# Revit family: KRS_вытяжка
name_source: partatom
category: Воздухораспределители
revit_build: Autodesk Revit 2014 (Build: 20130308_1515(x64)
units: mm (PartAtom-declared; Revit-internal decimal feet)

## types (459) — shared parameters
A = 23 мм
URL = inplast.ru
margins = 13 мм
Изготовитель = ИНПЛАСТ
Материал = Алюминий_RAL9016 (INPLAST)
Описание = Потолочная растровая решетка
Тип крепежа = саморезы
zero-valued in all types: Вес, кг

## per-type parameters (varying)
| type | Aef | C | C' | D | D' | n1 | n2 |
| KRS 100х100-АL-RAL9016 | 0.006 м² | 100 мм | 96 мм | 100 мм | 96 мм | 7 | 7 |
| KRS 125х100-АL-RAL9016 | 0.008 м² | 125 мм | 121 мм | 100 мм | 96 мм | 9 | 7 |
| KRS 125х125-АL-RAL9016 | 0.009 м² | 125 мм | 121 мм | 125 мм | 121 мм | 9 | 9 |
| KRS 150х100-АL-RAL9016 | 0.009 м² | 150 мм | 146 мм | 100 мм | 96 мм | 11 | 7 |
| KRS 150х125-АL-RAL9016 | 0.011 м² | 150 мм | 146 мм | 125 мм | 121 мм | 11 | 9 |
| KRS 150х150-АL-RAL9016 | 0.014 м² | 150 мм | 146 мм | 150 мм | 146 мм | 11 | 11 |
| KRS 200х100-АL-RAL9016 | 0.012 м² | 200 мм | 196 мм | 100 мм | 96 мм | 14 | 7 |
| KRS 200х125-АL-RAL9016 | 0.015 м² | 200 мм | 196 мм | 125 мм | 121 мм | 14 | 9 |
| KRS 200х150-АL-RAL9016 | 0.018 м² | 200 мм | 196 мм | 150 мм | 146 мм | 14 | 11 |
| KRS 200х200-АL-RAL9016 | 0.024 м² | 200 мм | 196 мм | 200 мм | 196 мм | 14 | 14 |
| KRS 225х100-АL-RAL9016 | 0.014 м² | 225 мм | 221 мм | 100 мм | 96 мм | 16 | 7 |
| KRS 225х125-АL-RAL9016 | 0.017 м² | 225 мм | 221 мм | 125 мм | 121 мм | 16 | 9 |
| KRS 225х150-АL-RAL9016 | 0.020 м² | 225 мм | 221 мм | 150 мм | 146 мм | 16 | 11 |
| KRS 225х200-АL-RAL9016 | 0.027 м² | 225 мм | 221 мм | 200 мм | 196 мм | 16 | 14 |
| KRS 225х225-АL-RAL9016 | 0.030 м² | 225 мм | 221 мм | 225 мм | 221 мм | 16 | 16 |
| KRS 250х100-АL-RAL9016 | 0.015 м² | 250 мм | 246 мм | 100 мм | 96 мм | 18 | 7 |
| KRS 250х125-АL-RAL9016 | 0.019 м² | 250 мм | 246 мм | 125 мм | 121 мм | 18 | 9 |
| KRS 250х150-АL-RAL9016 | 0.023 м² | 250 мм | 246 мм | 150 мм | 146 мм | 18 | 11 |
| KRS 250х200-АL-RAL9016 | 0.030 м² | 250 мм | 246 мм | 200 мм | 196 мм | 18 | 14 |
| KRS 250х225-АL-RAL9016 | 0.034 м² | 250 мм | 246 мм | 225 мм | 221 мм | 18 | 16 |
| KRS 250х250-АL-RAL9016 | 0.038 м² | 250 мм | 246 мм | 250 мм | 246 мм | 18 | 18 |
| KRS 300х100-АL-RAL9016 | 0.018 м² | 300 мм | 296 мм | 100 мм | 96 мм | 21 | 7 |
| KRS 300х125-АL-RAL9016 | 0.023 м² | 300 мм | 296 мм | 125 мм | 121 мм | 21 | 9 |
| KRS 300х150-АL-RAL9016 | 0.027 м² | 300 мм | 296 мм | 150 мм | 146 мм | 21 | 11 |
| KRS 300х200-АL-RAL9016 | 0.036 м² | 300 мм | 296 мм | 200 мм | 196 мм | 21 | 14 |
| KRS 300х225-АL-RAL9016 | 0.041 м² | 300 мм | 296 мм | 225 мм | 221 мм | 21 | 16 |
| KRS 300х250-АL-RAL9016 | 0.045 м² | 300 мм | 296 мм | 250 мм | 246 мм | 21 | 18 |
| KRS 300х300-АL-RAL9016 | 0.054 м² | 300 мм | 296 мм | 300 мм | 296 мм | 21 | 21 |
| KRS 325х100-АL-RAL9016 | 0.020 м² | 325 мм | 321 мм | 100 мм | 96 мм | 23 | 7 |
| KRS 325х125-АL-RAL9016 | 0.024 м² | 325 мм | 321 мм | 125 мм | 121 мм | 23 | 9 |
| KRS 325х150-АL-RAL9016 | 0.029 м² | 325 мм | 321 мм | 150 мм | 146 мм | 23 | 11 |
| KRS 325х200-АL-RAL9016 | 0.039 м² | 325 мм | 321 мм | 200 мм | 196 мм | 23 | 14 |
| KRS 325х225-АL-RAL9016 | 0.044 м² | 325 мм | 321 мм | 225 мм | 221 мм | 23 | 16 |
| KRS 325х250-АL-RAL9016 | 0.049 м² | 325 мм | 321 мм | 250 мм | 246 мм | 23 | 18 |
| KRS 325х300-АL-RAL9016 | 0.059 м² | 325 мм | 321 мм | 300 мм | 296 мм | 23 | 21 |
| KRS 325х325-АL-RAL9016 | 0.064 м² | 325 мм | 321 мм | 325 мм | 321 мм | 23 | 23 |
| KRS 350х100-АL-RAL9016 | 0.021 м² | 350 мм | 346 мм | 100 мм | 96 мм | 25 | 7 |
| KRS 350х125-АL-RAL9016 | 0.026 м² | 350 мм | 346 мм | 125 мм | 121 мм | 25 | 9 |
| KRS 350х150-АL-RAL9016 | 0.032 м² | 350 мм | 346 мм | 150 мм | 146 мм | 25 | 11 |
| KRS 350х200-АL-RAL9016 | 0.042 м² | 350 мм | 346 мм | 200 мм | 196 мм | 25 | 14 |
| KRS 350х225-АL-RAL9016 | 0.047 м² | 350 мм | 346 мм | 225 мм | 221 мм | 25 | 16 |
| KRS 350х250-АL-RAL9016 | 0.053 м² | 350 мм | 346 мм | 250 мм | 246 мм | 25 | 18 |
| KRS 350х300-АL-RAL9016 | 0.063 м² | 350 мм | 346 мм | 300 мм | 296 мм | 25 | 21 |
| KRS 350х325-АL-RAL9016 | 0.068 м² | 350 мм | 346 мм | 325 мм | 321 мм | 25 | 23 |
| KRS 350х350-АL-RAL9016 | 0.074 м² | 350 мм | 346 мм | 350 мм | 346 мм | 25 | 25 |
| KRS 400х100-АL-RAL9016 | 0.024 м² | 400 мм | 396 мм | 100 мм | 96 мм | 29 | 7 |
| KRS 400х125-АL-RAL9016 | 0.030 м² | 400 мм | 396 мм | 125 мм | 121 мм | 29 | 9 |
| KRS 400х150-АL-RAL9016 | 0.036 м² | 400 мм | 396 мм | 150 мм | 146 мм | 29 | 11 |
| KRS 400х200-АL-RAL9016 | 0.048 м² | 400 мм | 396 мм | 200 мм | 196 мм | 29 | 14 |
| KRS 400х225-АL-RAL9016 | 0.054 м² | 400 мм | 396 мм | 225 мм | 221 мм | 29 | 16 |
| KRS 400х250-АL-RAL9016 | 0.060 м² | 400 мм | 396 мм | 250 мм | 246 мм | 29 | 18 |
| KRS 400х300-АL-RAL9016 | 0.072 м² | 400 мм | 396 мм | 300 мм | 296 мм | 29 | 21 |
| KRS 400х325-АL-RAL9016 | 0.078 м² | 400 мм | 396 мм | 325 мм | 321 мм | 29 | 23 |
| KRS 400х350-АL-RAL9016 | 0.084 м² | 400 мм | 396 мм | 350 мм | 346 мм | 29 | 25 |
| KRS 400х400-АL-RAL9016 | 0.096 м² | 400 мм | 396 мм | 400 мм | 396 мм | 29 | 29 |
| KRS 425х100-АL-RAL9016 | 0.026 м² | 425 мм | 421 мм | 100 мм | 96 мм | 30 | 7 |
| KRS 425х125-АL-RAL9016 | 0.032 м² | 425 мм | 421 мм | 125 мм | 121 мм | 30 | 9 |
| KRS 425х150-АL-RAL9016 | 0.038 м² | 425 мм | 421 мм | 150 мм | 146 мм | 30 | 11 |
| KRS 425х200-АL-RAL9016 | 0.051 м² | 425 мм | 421 мм | 200 мм | 196 мм | 30 | 14 |
| KRS 425х225-АL-RAL9016 | 0.058 м² | 425 мм | 421 мм | 225 мм | 221 мм | 30 | 16 |
| KRS 425х250-АL-RAL9016 | 0.064 м² | 425 мм | 421 мм | 250 мм | 246 мм | 30 | 18 |
| KRS 425х300-АL-RAL9016 | 0.077 м² | 425 мм | 421 мм | 300 мм | 296 мм | 30 | 21 |
| KRS 425х325-АL-RAL9016 | 0.083 м² | 425 мм | 421 мм | 325 мм | 321 мм | 30 | 23 |
| KRS 425х350-АL-RAL9016 | 0.089 м² | 425 мм | 421 мм | 350 мм | 346 мм | 30 | 25 |
| KRS 425х400-АL-RAL9016 | 0.102 м² | 425 мм | 421 мм | 400 мм | 396 мм | 30 | 29 |
| KRS 425х425-АL-RAL9016 | 0.109 м² | 425 мм | 421 мм | 425 мм | 421 мм | 30 | 30 |
| KRS 450х100-АL-RAL9016 | 0.027 м² | 450 мм | 446 мм | 100 мм | 96 мм | 32 | 7 |
| KRS 450х125-АL-RAL9016 | 0.034 м² | 450 мм | 446 мм | 125 мм | 121 мм | 32 | 9 |
| KRS 450х150-АL-RAL9016 | 0.041 м² | 450 мм | 446 мм | 150 мм | 146 мм | 32 | 11 |
| KRS 450х200-АL-RAL9016 | 0.054 м² | 450 мм | 446 мм | 200 мм | 196 мм | 32 | 14 |
| KRS 450х225-АL-RAL9016 | 0.061 м² | 450 мм | 446 мм | 225 мм | 221 мм | 32 | 16 |
| KRS 450х250-АL-RAL9016 | 0.068 м² | 450 мм | 446 мм | 250 мм | 246 мм | 32 | 18 |
| KRS 450х300-АL-RAL9016 | 0.081 м² | 450 мм | 446 мм | 300 мм | 296 мм | 32 | 21 |
| KRS 450х325-АL-RAL9016 | 0.088 м² | 450 мм | 446 мм | 325 мм | 321 мм | 32 | 23 |
| KRS 450х350-АL-RAL9016 | 0.095 м² | 450 мм | 446 мм | 350 мм | 346 мм | 32 | 25 |
| KRS 450х400-АL-RAL9016 | 0.108 м² | 450 мм | 446 мм | 400 мм | 396 мм | 32 | 29 |
| KRS 450х425-АL-RAL9016 | 0.115 м² | 450 мм | 446 мм | 425 мм | 421 мм | 32 | 30 |
| KRS 450х450-АL-RAL9016 | 0.122 м² | 450 мм | 446 мм | 450 мм | 446 мм | 32 | 32 |
| KRS 500х100-АL-RAL9016 | 0.030 м² | 500 мм | 496 мм | 100 мм | 96 мм | 36 | 7 |
| KRS 500х125-АL-RAL9016 | 0.038 м² | 500 мм | 496 мм | 125 мм | 121 мм | 36 | 9 |
| KRS 500х150-АL-RAL9016 | 0.045 м² | 500 мм | 496 мм | 150 мм | 146 мм | 36 | 11 |
| KRS 500х200-АL-RAL9016 | 0.060 м² | 500 мм | 496 мм | 200 мм | 196 мм | 36 | 14 |
| KRS 500х225-АL-RAL9016 | 0.068 м² | 500 мм | 496 мм | 225 мм | 221 мм | 36 | 16 |
| KRS 500х250-АL-RAL9016 | 0.075 м² | 500 мм | 496 мм | 250 мм | 246 мм | 36 | 18 |
| KRS 500х300-АL-RAL9016 | 0.090 м² | 500 мм | 496 мм | 300 мм | 296 мм | 36 | 21 |
| KRS 500х325-АL-RAL9016 | 0.098 м² | 500 мм | 496 мм | 325 мм | 321 мм | 36 | 23 |
| KRS 500х350-АL-RAL9016 | 0.105 м² | 500 мм | 496 мм | 350 мм | 346 мм | 36 | 25 |
| KRS 500х400-АL-RAL9016 | 0.120 м² | 500 мм | 496 мм | 400 мм | 396 мм | 36 | 29 |
| KRS 500х425-АL-RAL9016 | 0.128 м² | 500 мм | 496 мм | 425 мм | 421 мм | 36 | 30 |
| KRS 500х450-АL-RAL9016 | 0.135 м² | 500 мм | 496 мм | 450 мм | 446 мм | 36 | 32 |
| KRS 500х500-АL-RAL9016 | 0.150 м² | 500 мм | 496 мм | 500 мм | 496 мм | 36 | 36 |
| KRS 525х100-АL-RAL9016 | 0.032 м² | 525 мм | 521 мм | 100 мм | 96 мм | 38 | 7 |
| KRS 525х125-АL-RAL9016 | 0.039 м² | 525 мм | 521 мм | 125 мм | 121 мм | 38 | 9 |
| KRS 525х150-АL-RAL9016 | 0.047 м² | 525 мм | 521 мм | 150 мм | 146 мм | 38 | 11 |
| KRS 525х200-АL-RAL9016 | 0.063 м² | 525 мм | 521 мм | 200 мм | 196 мм | 38 | 14 |
| KRS 525х225-АL-RAL9016 | 0.071 м² | 525 мм | 521 мм | 225 мм | 221 мм | 38 | 16 |
| KRS 525х250-АL-RAL9016 | 0.079 м² | 525 мм | 521 мм | 250 мм | 246 мм | 38 | 18 |
| KRS 525х300-АL-RAL9016 | 0.095 м² | 525 мм | 521 мм | 300 мм | 296 мм | 38 | 21 |
| KRS 525х325-АL-RAL9016 | 0.103 м² | 525 мм | 521 мм | 325 мм | 321 мм | 38 | 23 |
| KRS 525х350-АL-RAL9016 | 0.111 м² | 525 мм | 521 мм | 350 мм | 346 мм | 38 | 25 |
| KRS 525х400-АL-RAL9016 | 0.126 м² | 525 мм | 521 мм | 400 мм | 396 мм | 38 | 29 |
| KRS 525х425-АL-RAL9016 | 0.134 м² | 525 мм | 521 мм | 425 мм | 421 мм | 38 | 30 |
| KRS 525х450-АL-RAL9016 | 0.142 м² | 525 мм | 521 мм | 450 мм | 446 мм | 38 | 32 |
| KRS 525х500-АL-RAL9016 | 0.158 м² | 525 мм | 521 мм | 500 мм | 496 мм | 38 | 36 |
| KRS 525х525-АL-RAL9016 | 0.166 м² | 525 мм | 521 мм | 525 мм | 521 мм | 38 | 38 |
| KRS 550х100-АL-RAL9016 | 0.033 м² | 550 мм | 546 мм | 100 мм | 96 мм | 39 | 7 |
| KRS 550х125-АL-RAL9016 | 0.041 м² | 550 мм | 546 мм | 125 мм | 121 мм | 39 | 9 |
| KRS 550х150-АL-RAL9016 | 0.050 м² | 550 мм | 546 мм | 150 мм | 146 мм | 39 | 11 |
| KRS 550х200-АL-RAL9016 | 0.066 м² | 550 мм | 546 мм | 200 мм | 196 мм | 39 | 14 |
| KRS 550х225-АL-RAL9016 | 0.074 м² | 550 мм | 546 мм | 225 мм | 221 мм | 39 | 16 |
| KRS 550х250-АL-RAL9016 | 0.083 м² | 550 мм | 546 мм | 250 мм | 246 мм | 39 | 18 |
| KRS 550х300-АL-RAL9016 | 0.099 м² | 550 мм | 546 мм | 300 мм | 296 мм | 39 | 21 |
| KRS 550х325-АL-RAL9016 | 0.108 м² | 550 мм | 546 мм | 325 мм | 321 мм | 39 | 23 |
| KRS 550х350-АL-RAL9016 | 0.116 м² | 550 мм | 546 мм | 350 мм | 346 мм | 39 | 25 |
| KRS 550х400-АL-RAL9016 | 0.132 м² | 550 мм | 546 мм | 400 мм | 396 мм | 39 | 29 |
| KRS 550х425-АL-RAL9016 | 0.141 м² | 550 мм | 546 мм | 425 мм | 421 мм | 39 | 30 |
| KRS 550х450-АL-RAL9016 | 0.149 м² | 550 мм | 546 мм | 450 мм | 446 мм | 39 | 32 |
| KRS 550х500-АL-RAL9016 | 0.165 м² | 550 мм | 546 мм | 500 мм | 496 мм | 39 | 36 |
| KRS 550х525-АL-RAL9016 | 0.174 м² | 550 мм | 546 мм | 525 мм | 521 мм | 39 | 38 |
| KRS 550х550-АL-RAL9016 | 0.182 м² | 550 мм | 546 мм | 550 мм | 546 мм | 39 | 39 |
| KRS 600х100-АL-RAL9016 | 0.036 м² | 600 мм | 596 мм | 100 мм | 96 мм | 43 | 7 |
| KRS 600х125-АL-RAL9016 | 0.045 м² | 600 мм | 596 мм | 125 мм | 121 мм | 43 | 9 |
| KRS 600х150-АL-RAL9016 | 0.054 м² | 600 мм | 596 мм | 150 мм | 146 мм | 43 | 11 |
| KRS 600х200-АL-RAL9016 | 0.072 м² | 600 мм | 596 мм | 200 мм | 196 мм | 43 | 14 |
| KRS 600х225-АL-RAL9016 | 0.081 м² | 600 мм | 596 мм | 225 мм | 221 мм | 43 | 16 |
| KRS 600х250-АL-RAL9016 | 0.090 м² | 600 мм | 596 мм | 250 мм | 246 мм | 43 | 18 |
| KRS 600х300-АL-RAL9016 | 0.108 м² | 600 мм | 596 мм | 300 мм | 296 мм | 43 | 21 |
| KRS 600х325-АL-RAL9016 | 0.117 м² | 600 мм | 596 мм | 325 мм | 321 мм | 43 | 23 |
| KRS 600х350-АL-RAL9016 | 0.126 м² | 600 мм | 596 мм | 350 мм | 346 мм | 43 | 25 |
| KRS 600х400-АL-RAL9016 | 0.144 м² | 600 мм | 596 мм | 400 мм | 396 мм | 43 | 29 |
| KRS 600х425-АL-RAL9016 | 0.153 м² | 600 мм | 596 мм | 425 мм | 421 мм | 43 | 30 |
| KRS 600х450-АL-RAL9016 | 0.162 м² | 600 мм | 596 мм | 450 мм | 446 мм | 43 | 32 |
| KRS 600х500-АL-RAL9016 | 0.180 м² | 600 мм | 596 мм | 500 мм | 496 мм | 43 | 36 |
| KRS 600х525-АL-RAL9016 | 0.190 м² | 600 мм | 596 мм | 525 мм | 521 мм | 43 | 38 |
| KRS 600х550-АL-RAL9016 | 0.199 м² | 600 мм | 596 мм | 550 мм | 546 мм | 43 | 39 |
| KRS 600х600-АL-RAL9016 | 0.217 м² | 600 мм | 596 мм | 600 мм | 596 мм | 43 | 43 |
| KRS 625х100-АL-RAL9016 | 0.038 м² | 625 мм | 621 мм | 100 мм | 96 мм | 45 | 7 |
| KRS 625х125-АL-RAL9016 | 0.047 м² | 625 мм | 621 мм | 125 мм | 121 мм | 45 | 9 |
| KRS 625х150-АL-RAL9016 | 0.056 м² | 625 мм | 621 мм | 150 мм | 146 мм | 45 | 11 |
| KRS 625х200-АL-RAL9016 | 0.075 м² | 625 мм | 621 мм | 200 мм | 196 мм | 45 | 14 |
| KRS 625х225-АL-RAL9016 | 0.085 м² | 625 мм | 621 мм | 225 мм | 221 мм | 45 | 16 |
| KRS 625х250-АL-RAL9016 | 0.094 м² | 625 мм | 621 мм | 250 мм | 246 мм | 45 | 18 |
| KRS 625х300-АL-RAL9016 | 0.113 м² | 625 мм | 621 мм | 300 мм | 296 мм | 45 | 21 |
| KRS 625х325-АL-RAL9016 | 0.122 м² | 625 мм | 621 мм | 325 мм | 321 мм | 45 | 23 |
| KRS 625х350-АL-RAL9016 | 0.132 м² | 625 мм | 621 мм | 350 мм | 346 мм | 45 | 25 |
| KRS 625х400-АL-RAL9016 | 0.150 м² | 625 мм | 621 мм | 400 мм | 396 мм | 45 | 29 |
| KRS 625х425-АL-RAL9016 | 0.160 м² | 625 мм | 621 мм | 425 мм | 421 мм | 45 | 30 |
| KRS 625х450-АL-RAL9016 | 0.169 м² | 625 мм | 621 мм | 450 мм | 446 мм | 45 | 32 |
| KRS 625х500-АL-RAL9016 | 0.188 м² | 625 мм | 621 мм | 500 мм | 496 мм | 45 | 36 |
| KRS 625х525-АL-RAL9016 | 0.197 м² | 625 мм | 621 мм | 525 мм | 521 мм | 45 | 38 |
| KRS 625х550-АL-RAL9016 | 0.207 м² | 625 мм | 621 мм | 550 мм | 546 мм | 45 | 39 |
| KRS 625х600-АL-RAL9016 | 0.226 м² | 625 мм | 621 мм | 600 мм | 596 мм | 45 | 43 |
| KRS 625х625-АL-RAL9016 | 0.235 м² | 625 мм | 621 мм | 625 мм | 621 мм | 45 | 45 |
| KRS 650х100-АL-RAL9016 | 0.039 м² | 650 мм | 646 мм | 100 мм | 96 мм | 46 | 7 |
| KRS 650х125-АL-RAL9016 | 0.049 м² | 650 мм | 646 мм | 125 мм | 121 мм | 46 | 9 |
| KRS 650х150-АL-RAL9016 | 0.059 м² | 650 мм | 646 мм | 150 мм | 146 мм | 46 | 11 |
| KRS 650х200-АL-RAL9016 | 0.078 м² | 650 мм | 646 мм | 200 мм | 196 мм | 46 | 14 |
| KRS 650х225-АL-RAL9016 | 0.088 м² | 650 мм | 646 мм | 225 мм | 221 мм | 46 | 16 |
| KRS 650х250-АL-RAL9016 | 0.098 м² | 650 мм | 646 мм | 250 мм | 246 мм | 46 | 18 |
| KRS 650х300-АL-RAL9016 | 0.117 м² | 650 мм | 646 мм | 300 мм | 296 мм | 46 | 21 |
| KRS 650х325-АL-RAL9016 | 0.127 м² | 650 мм | 646 мм | 325 мм | 321 мм | 46 | 23 |
| KRS 650х350-АL-RAL9016 | 0.137 м² | 650 мм | 646 мм | 350 мм | 346 мм | 46 | 25 |
| KRS 650х400-АL-RAL9016 | 0.156 м² | 650 мм | 646 мм | 400 мм | 396 мм | 46 | 29 |
| KRS 650х425-АL-RAL9016 | 0.166 м² | 650 мм | 646 мм | 425 мм | 421 мм | 46 | 30 |
| KRS 650х450-АL-RAL9016 | 0.176 м² | 650 мм | 646 мм | 450 мм | 446 мм | 46 | 32 |
| KRS 650х500-АL-RAL9016 | 0.196 м² | 650 мм | 646 мм | 500 мм | 496 мм | 46 | 36 |
| KRS 650х525-АL-RAL9016 | 0.205 м² | 650 мм | 646 мм | 525 мм | 521 мм | 46 | 38 |
| KRS 650х550-АL-RAL9016 | 0.215 м² | 650 мм | 646 мм | 550 мм | 546 мм | 46 | 39 |
| KRS 650х600-АL-RAL9016 | 0.235 м² | 650 мм | 646 мм | 600 мм | 596 мм | 46 | 43 |
| KRS 650х625-АL-RAL9016 | 0.244 м² | 650 мм | 646 мм | 625 мм | 621 мм | 46 | 45 |
| KRS 700х100-АL-RAL9016 | 0.042 м² | 700 мм | 696 мм | 100 мм | 96 мм | 50 | 7 |
| KRS 700х125-АL-RAL9016 | 0.053 м² | 700 мм | 696 мм | 125 мм | 121 мм | 50 | 9 |
| KRS 700х150-АL-RAL9016 | 0.063 м² | 700 мм | 696 мм | 150 мм | 146 мм | 50 | 11 |
| KRS 700х200-АL-RAL9016 | 0.084 м² | 700 мм | 696 мм | 200 мм | 196 мм | 50 | 14 |
| KRS 700х225-АL-RAL9016 | 0.095 м² | 700 мм | 696 мм | 225 мм | 221 мм | 50 | 16 |
| KRS 700х250-АL-RAL9016 | 0.105 м² | 700 мм | 696 мм | 250 мм | 246 мм | 50 | 18 |
| KRS 700х300-АL-RAL9016 | 0.126 м² | 700 мм | 696 мм | 300 мм | 296 мм | 50 | 21 |
| KRS 700х325-АL-RAL9016 | 0.137 м² | 700 мм | 696 мм | 325 мм | 321 мм | 50 | 23 |
| KRS 700х350-АL-RAL9016 | 0.147 м² | 700 мм | 696 мм | 350 мм | 346 мм | 50 | 25 |
| KRS 700х400-АL-RAL9016 | 0.168 м² | 700 мм | 696 мм | 400 мм | 396 мм | 50 | 29 |
| KRS 700х425-АL-RAL9016 | 0.179 м² | 700 мм | 696 мм | 425 мм | 421 мм | 50 | 30 |
| KRS 700х450-АL-RAL9016 | 0.190 м² | 700 мм | 696 мм | 450 мм | 446 мм | 50 | 32 |
| KRS 700х500-АL-RAL9016 | 0.211 м² | 700 мм | 696 мм | 500 мм | 496 мм | 50 | 36 |
| KRS 700х525-АL-RAL9016 | 0.221 м² | 700 мм | 696 мм | 525 мм | 521 мм | 50 | 38 |
| KRS 700х550-АL-RAL9016 | 0.232 м² | 700 мм | 696 мм | 550 мм | 546 мм | 50 | 39 |
| KRS 700х600-АL-RAL9016 | 0.253 м² | 700 мм | 696 мм | 600 мм | 596 мм | 50 | 43 |
| KRS 700х625-АL-RAL9016 | 0.263 м² | 700 мм | 696 мм | 625 мм | 621 мм | 50 | 45 |
| KRS 725х100-АL-RAL9016 | 0.044 м² | 725 мм | 721 мм | 100 мм | 96 мм | 52 | 7 |
| KRS 725х125-АL-RAL9016 | 0.055 м² | 725 мм | 721 мм | 125 мм | 121 мм | 52 | 9 |
| KRS 725х150-АL-RAL9016 | 0.065 м² | 725 мм | 721 мм | 150 мм | 146 мм | 52 | 11 |
| KRS 725х200-АL-RAL9016 | 0.087 м² | 725 мм | 721 мм | 200 мм | 196 мм | 52 | 14 |
| KRS 725х225-АL-RAL9016 | 0.098 м² | 725 мм | 721 мм | 225 мм | 221 мм | 52 | 16 |
| KRS 725х250-АL-RAL9016 | 0.109 м² | 725 мм | 721 мм | 250 мм | 246 мм | 52 | 18 |
| KRS 725х300-АL-RAL9016 | 0.131 м² | 725 мм | 721 мм | 300 мм | 296 мм | 52 | 21 |
| KRS 725х325-АL-RAL9016 | 0.142 м² | 725 мм | 721 мм | 325 мм | 321 мм | 52 | 23 |
| KRS 725х350-АL-RAL9016 | 0.153 м² | 725 мм | 721 мм | 350 мм | 346 мм | 52 | 25 |
| KRS 725х400-АL-RAL9016 | 0.174 м² | 725 мм | 721 мм | 400 мм | 396 мм | 52 | 29 |
| KRS 725х425-АL-RAL9016 | 0.185 м² | 725 мм | 721 мм | 425 мм | 421 мм | 52 | 30 |
| KRS 725х450-АL-RAL9016 | 0.196 м² | 725 мм | 721 мм | 450 мм | 446 мм | 52 | 32 |
| KRS 725х500-АL-RAL9016 | 0.218 м² | 725 мм | 721 мм | 500 мм | 496 мм | 52 | 36 |
| KRS 725х525-АL-RAL9016 | 0.229 м² | 725 мм | 721 мм | 525 мм | 521 мм | 52 | 38 |
| KRS 725х550-АL-RAL9016 | 0.240 м² | 725 мм | 721 мм | 550 мм | 546 мм | 52 | 39 |
| KRS 725х600-АL-RAL9016 | 0.262 м² | 725 мм | 721 мм | 600 мм | 596 мм | 52 | 43 |
| KRS 725х625-АL-RAL9016 | 0.273 м² | 725 мм | 721 мм | 625 мм | 621 мм | 52 | 45 |
| KRS 750х100-АL-RAL9016 | 0.045 м² | 750 мм | 746 мм | 100 мм | 96 мм | 54 | 7 |
| KRS 750х125-АL-RAL9016 | 0.056 м² | 750 мм | 746 мм | 125 мм | 121 мм | 54 | 9 |
| KRS 750х150-АL-RAL9016 | 0.068 м² | 750 мм | 746 мм | 150 мм | 146 мм | 54 | 11 |
| KRS 750х200-АL-RAL9016 | 0.090 м² | 750 мм | 746 мм | 200 мм | 196 мм | 54 | 14 |
| KRS 750х225-АL-RAL9016 | 0.102 м² | 750 мм | 746 мм | 225 мм | 221 мм | 54 | 16 |
| KRS 750х250-АL-RAL9016 | 0.113 м² | 750 мм | 746 мм | 250 мм | 246 мм | 54 | 18 |
| KRS 750х300-АL-RAL9016 | 0.135 м² | 750 мм | 746 мм | 300 мм | 296 мм | 54 | 21 |
| KRS 750х325-АL-RAL9016 | 0.147 м² | 750 мм | 746 мм | 325 мм | 321 мм | 54 | 23 |
| KRS 750х350-АL-RAL9016 | 0.158 м² | 750 мм | 746 мм | 350 мм | 346 мм | 54 | 25 |
| KRS 750х400-АL-RAL9016 | 0.180 м² | 750 мм | 746 мм | 400 мм | 396 мм | 54 | 29 |
| KRS 750х425-АL-RAL9016 | 0.192 м² | 750 мм | 746 мм | 425 мм | 421 мм | 54 | 30 |
| KRS 750х450-АL-RAL9016 | 0.203 м² | 750 мм | 746 мм | 450 мм | 446 мм | 54 | 32 |
| KRS 750х500-АL-RAL9016 | 0.226 м² | 750 мм | 746 мм | 500 мм | 496 мм | 54 | 36 |
| KRS 750х525-АL-RAL9016 | 0.237 м² | 750 мм | 746 мм | 525 мм | 521 мм | 54 | 38 |
| KRS 750х550-АL-RAL9016 | 0.248 м² | 750 мм | 746 мм | 550 мм | 546 мм | 54 | 39 |
| KRS 750х600-АL-RAL9016 | 0.271 м² | 750 мм | 746 мм | 600 мм | 596 мм | 54 | 43 |
| KRS 750х625-АL-RAL9016 | 0.282 м² | 750 мм | 746 мм | 625 мм | 621 мм | 54 | 45 |
| KRS 800х100-АL-RAL9016 | 0.048 м² | 800 мм | 796 мм | 100 мм | 96 мм | 57 | 7 |
| KRS 800х125-АL-RAL9016 | 0.060 м² | 800 мм | 796 мм | 125 мм | 121 мм | 57 | 9 |
| KRS 800х150-АL-RAL9016 | 0.072 м² | 800 мм | 796 мм | 150 мм | 146 мм | 57 | 11 |
| KRS 800х200-АL-RAL9016 | 0.096 м² | 800 мм | 796 мм | 200 мм | 196 мм | 57 | 14 |
| KRS 800х225-АL-RAL9016 | 0.108 м² | 800 мм | 796 мм | 225 мм | 221 мм | 57 | 16 |
| KRS 800х250-АL-RAL9016 | 0.120 м² | 800 мм | 796 мм | 250 мм | 246 мм | 57 | 18 |
| KRS 800х300-АL-RAL9016 | 0.144 м² | 800 мм | 796 мм | 300 мм | 296 мм | 57 | 21 |
| KRS 800х325-АL-RAL9016 | 0.156 м² | 800 мм | 796 мм | 325 мм | 321 мм | 57 | 23 |
| KRS 800х350-АL-RAL9016 | 0.168 м² | 800 мм | 796 мм | 350 мм | 346 мм | 57 | 25 |
| KRS 800х400-АL-RAL9016 | 0.193 м² | 800 мм | 796 мм | 400 мм | 396 мм | 57 | 29 |
| KRS 800х425-АL-RAL9016 | 0.205 м² | 800 мм | 796 мм | 425 мм | 421 мм | 57 | 30 |
| KRS 800х450-АL-RAL9016 | 0.217 м² | 800 мм | 796 мм | 450 мм | 446 мм | 57 | 32 |
| KRS 800х500-АL-RAL9016 | 0.241 м² | 800 мм | 796 мм | 500 мм | 496 мм | 57 | 36 |
| KRS 800х525-АL-RAL9016 | 0.253 м² | 800 мм | 796 мм | 525 мм | 521 мм | 57 | 38 |
| KRS 800х550-АL-RAL9016 | 0.265 м² | 800 мм | 796 мм | 550 мм | 546 мм | 57 | 39 |
| KRS 800х600-АL-RAL9016 | 0.289 м² | 800 мм | 796 мм | 600 мм | 596 мм | 57 | 43 |
| KRS 800х625-АL-RAL9016 | 0.301 м² | 800 мм | 796 мм | 625 мм | 621 мм | 57 | 45 |
| KRS 825х100-АL-RAL9016 | 0.050 м² | 825 мм | 821 мм | 100 мм | 96 мм | 59 | 7 |
| KRS 825х125-АL-RAL9016 | 0.062 м² | 825 мм | 821 мм | 125 мм | 121 мм | 59 | 9 |
| KRS 825х150-АL-RAL9016 | 0.074 м² | 825 мм | 821 мм | 150 мм | 146 мм | 59 | 11 |
| KRS 825х200-АL-RAL9016 | 0.099 м² | 825 мм | 821 мм | 200 мм | 196 мм | 59 | 14 |
| KRS 825х225-АL-RAL9016 | 0.112 м² | 825 мм | 821 мм | 225 мм | 221 мм | 59 | 16 |
| KRS 825х250-АL-RAL9016 | 0.124 м² | 825 мм | 821 мм | 250 мм | 246 мм | 59 | 18 |
| KRS 825х300-АL-RAL9016 | 0.149 м² | 825 мм | 821 мм | 300 мм | 296 мм | 59 | 21 |
| KRS 825х325-АL-RAL9016 | 0.161 м² | 825 мм | 821 мм | 325 мм | 321 мм | 59 | 23 |
| KRS 825х350-АL-RAL9016 | 0.174 м² | 825 мм | 821 мм | 350 мм | 346 мм | 59 | 25 |
| KRS 825х400-АL-RAL9016 | 0.199 м² | 825 мм | 821 мм | 400 мм | 396 мм | 59 | 29 |
| KRS 825х425-АL-RAL9016 | 0.211 м² | 825 мм | 821 мм | 425 мм | 421 мм | 59 | 30 |
| KRS 825х450-АL-RAL9016 | 0.223 м² | 825 мм | 821 мм | 450 мм | 446 мм | 59 | 32 |
| KRS 825х500-АL-RAL9016 | 0.248 м² | 825 мм | 821 мм | 500 мм | 496 мм | 59 | 36 |
| KRS 825х525-АL-RAL9016 | 0.261 м² | 825 мм | 821 мм | 525 мм | 521 мм | 59 | 38 |
| KRS 825х550-АL-RAL9016 | 0.273 м² | 825 мм | 821 мм | 550 мм | 546 мм | 59 | 39 |
| KRS 825х600-АL-RAL9016 | 0.298 м² | 825 мм | 821 мм | 600 мм | 596 мм | 59 | 43 |
| KRS 825х625-АL-RAL9016 | 0.310 м² | 825 мм | 821 мм | 625 мм | 621 мм | 59 | 45 |
| KRS 850х100-АL-RAL9016 | 0.051 м² | 850 мм | 846 мм | 100 мм | 96 мм | 61 | 7 |
| KRS 850х125-АL-RAL9016 | 0.064 м² | 850 мм | 846 мм | 125 мм | 121 мм | 61 | 9 |
| KRS 850х150-АL-RAL9016 | 0.077 м² | 850 мм | 846 мм | 150 мм | 146 мм | 61 | 11 |
| KRS 850х200-АL-RAL9016 | 0.102 м² | 850 мм | 846 мм | 200 мм | 196 мм | 61 | 14 |
| KRS 850х225-АL-RAL9016 | 0.115 м² | 850 мм | 846 мм | 225 мм | 221 мм | 61 | 16 |
| KRS 850х250-АL-RAL9016 | 0.128 м² | 850 мм | 846 мм | 250 мм | 246 мм | 61 | 18 |
| KRS 850х300-АL-RAL9016 | 0.153 м² | 850 мм | 846 мм | 300 мм | 296 мм | 61 | 21 |
| KRS 850х325-АL-RAL9016 | 0.166 м² | 850 мм | 846 мм | 325 мм | 321 мм | 61 | 23 |
| KRS 850х350-АL-RAL9016 | 0.179 м² | 850 мм | 846 мм | 350 мм | 346 мм | 61 | 25 |
| KRS 850х400-АL-RAL9016 | 0.205 м² | 850 мм | 846 мм | 400 мм | 396 мм | 61 | 29 |
| KRS 850х425-АL-RAL9016 | 0.217 м² | 850 мм | 846 мм | 425 мм | 421 мм | 61 | 30 |
| KRS 850х450-АL-RAL9016 | 0.230 м² | 850 мм | 846 мм | 450 мм | 446 мм | 61 | 32 |
| KRS 850х500-АL-RAL9016 | 0.256 м² | 850 мм | 846 мм | 500 мм | 496 мм | 61 | 36 |
| KRS 850х525-АL-RAL9016 | 0.268 м² | 850 мм | 846 мм | 525 мм | 521 мм | 61 | 38 |
| KRS 850х550-АL-RAL9016 | 0.281 м² | 850 мм | 846 мм | 550 мм | 546 мм | 61 | 39 |
| KRS 850х600-АL-RAL9016 | 0.307 м² | 850 мм | 846 мм | 600 мм | 596 мм | 61 | 43 |
| KRS 850х625-АL-RAL9016 | 0.320 м² | 850 мм | 846 мм | 625 мм | 621 мм | 61 | 45 |
| KRS 900х100-АL-RAL9016 | 0.054 м² | 900 мм | 896 мм | 100 мм | 96 мм | 64 | 7 |
| KRS 900х125-АL-RAL9016 | 0.068 м² | 900 мм | 896 мм | 125 мм | 121 мм | 64 | 9 |
| KRS 900х150-АL-RAL9016 | 0.081 м² | 900 мм | 896 мм | 150 мм | 146 мм | 64 | 11 |
| KRS 900х200-АL-RAL9016 | 0.108 м² | 900 мм | 896 мм | 200 мм | 196 мм | 64 | 14 |
| KRS 900х225-АL-RAL9016 | 0.122 м² | 900 мм | 896 мм | 225 мм | 221 мм | 64 | 16 |
| KRS 900х250-АL-RAL9016 | 0.135 м² | 900 мм | 896 мм | 250 мм | 246 мм | 64 | 18 |
| KRS 900х300-АL-RAL9016 | 0.162 м² | 900 мм | 896 мм | 300 мм | 296 мм | 64 | 21 |
| KRS 900х325-АL-RAL9016 | 0.176 м² | 900 мм | 896 мм | 325 мм | 321 мм | 64 | 23 |
| KRS 900х350-АL-RAL9016 | 0.190 м² | 900 мм | 896 мм | 350 мм | 346 мм | 64 | 25 |
| KRS 900х400-АL-RAL9016 | 0.217 м² | 900 мм | 896 мм | 400 мм | 396 мм | 64 | 29 |
| KRS 900х425-АL-RAL9016 | 0.230 м² | 900 мм | 896 мм | 425 мм | 421 мм | 64 | 30 |
| KRS 900х450-АL-RAL9016 | 0.244 м² | 900 мм | 896 мм | 450 мм | 446 мм | 64 | 32 |
| KRS 900х500-АL-RAL9016 | 0.271 м² | 900 мм | 896 мм | 500 мм | 496 мм | 64 | 36 |
| KRS 900х525-АL-RAL9016 | 0.284 м² | 900 мм | 896 мм | 525 мм | 521 мм | 64 | 38 |
| KRS 900х550-АL-RAL9016 | 0.298 м² | 900 мм | 896 мм | 550 мм | 546 мм | 64 | 39 |
| KRS 900х600-АL-RAL9016 | 0.325 м² | 900 мм | 896 мм | 600 мм | 596 мм | 64 | 43 |
| KRS 900х625-АL-RAL9016 | 0.338 м² | 900 мм | 896 мм | 625 мм | 621 мм | 64 | 45 |
| KRS 925х100-АL-RAL9016 | 0.056 м² | 925 мм | 921 мм | 100 мм | 96 мм | 66 | 7 |
| KRS 925х125-АL-RAL9016 | 0.070 м² | 925 мм | 921 мм | 125 мм | 121 мм | 66 | 9 |
| KRS 925х150-АL-RAL9016 | 0.083 м² | 925 мм | 921 мм | 150 мм | 146 мм | 66 | 11 |
| KRS 925х200-АL-RAL9016 | 0.111 м² | 925 мм | 921 мм | 200 мм | 196 мм | 66 | 14 |
| KRS 925х225-АL-RAL9016 | 0.125 м² | 925 мм | 921 мм | 225 мм | 221 мм | 66 | 16 |
| KRS 925х250-АL-RAL9016 | 0.139 м² | 925 мм | 921 мм | 250 мм | 246 мм | 66 | 18 |
| KRS 925х300-АL-RAL9016 | 0.167 м² | 925 мм | 921 мм | 300 мм | 296 мм | 66 | 21 |
| KRS 925х325-АL-RAL9016 | 0.181 м² | 925 мм | 921 мм | 325 мм | 321 мм | 66 | 23 |
| KRS 925х350-АL-RAL9016 | 0.195 м² | 925 мм | 921 мм | 350 мм | 346 мм | 66 | 25 |
| KRS 925х400-АL-RAL9016 | 0.223 м² | 925 мм | 921 мм | 400 мм | 396 мм | 66 | 29 |
| KRS 925х425-АL-RAL9016 | 0.237 м² | 925 мм | 921 мм | 425 мм | 421 мм | 66 | 30 |
| KRS 925х450-АL-RAL9016 | 0.250 м² | 925 мм | 921 мм | 450 мм | 446 мм | 66 | 32 |
| KRS 925х500-АL-RAL9016 | 0.278 м² | 925 мм | 921 мм | 500 мм | 496 мм | 66 | 36 |
| KRS 925х525-АL-RAL9016 | 0.292 м² | 925 мм | 921 мм | 525 мм | 521 мм | 66 | 38 |
| KRS 925х550-АL-RAL9016 | 0.306 м² | 925 мм | 921 мм | 550 мм | 546 мм | 66 | 39 |
| KRS 925х600-АL-RAL9016 | 0.334 м² | 925 мм | 921 мм | 600 мм | 596 мм | 66 | 43 |
| KRS 925х625-АL-RAL9016 | 0.348 м² | 925 мм | 921 мм | 625 мм | 621 мм | 66 | 45 |
| KRS 950х100-АL-RAL9016 | 0.057 м² | 950 мм | 946 мм | 100 мм | 96 мм | 68 | 7 |
| KRS 950х125-АL-RAL9016 | 0.071 м² | 950 мм | 946 мм | 125 мм | 121 мм | 68 | 9 |
| KRS 950х150-АL-RAL9016 | 0.086 м² | 950 мм | 946 мм | 150 мм | 146 мм | 68 | 11 |
| KRS 950х200-АL-RAL9016 | 0.114 м² | 950 мм | 946 мм | 200 мм | 196 мм | 68 | 14 |
| KRS 950х225-АL-RAL9016 | 0.129 м² | 950 мм | 946 мм | 225 мм | 221 мм | 68 | 16 |
| KRS 950х250-АL-RAL9016 | 0.143 м² | 950 мм | 946 мм | 250 мм | 246 мм | 68 | 18 |
| KRS 950х300-АL-RAL9016 | 0.171 м² | 950 мм | 946 мм | 300 мм | 296 мм | 68 | 21 |
| KRS 950х325-АL-RAL9016 | 0.186 м² | 950 мм | 946 мм | 325 мм | 321 мм | 68 | 23 |
| KRS 950х350-АL-RAL9016 | 0.200 м² | 950 мм | 946 мм | 350 мм | 346 мм | 68 | 25 |
| KRS 950х400-АL-RAL9016 | 0.229 м² | 950 мм | 946 мм | 400 мм | 396 мм | 68 | 29 |
| KRS 950х425-АL-RAL9016 | 0.243 м² | 950 мм | 946 мм | 425 мм | 421 мм | 68 | 30 |
| KRS 950х450-АL-RAL9016 | 0.257 м² | 950 мм | 946 мм | 450 мм | 446 мм | 68 | 32 |
| KRS 950х500-АL-RAL9016 | 0.286 м² | 950 мм | 946 мм | 500 мм | 496 мм | 68 | 36 |
| KRS 950х525-АL-RAL9016 | 0.300 м² | 950 мм | 946 мм | 525 мм | 521 мм | 68 | 38 |
| KRS 950х550-АL-RAL9016 | 0.314 м² | 950 мм | 946 мм | 550 мм | 546 мм | 68 | 39 |
| KRS 950х600-АL-RAL9016 | 0.343 м² | 950 мм | 946 мм | 600 мм | 596 мм | 68 | 43 |
| KRS 950х625-АL-RAL9016 | 0.357 м² | 950 мм | 946 мм | 625 мм | 621 мм | 68 | 45 |
| KRS 1000х100-АL-RAL9016 | 0.060 м² | 1000 мм | 996 мм | 100 мм | 96 мм | 71 | 7 |
| KRS 1000х125-АL-RAL9016 | 0.075 м² | 1000 мм | 996 мм | 125 мм | 121 мм | 71 | 9 |
| KRS 1000х150-АL-RAL9016 | 0.090 м² | 1000 мм | 996 мм | 150 мм | 146 мм | 71 | 11 |
| KRS 1000х200-АL-RAL9016 | 0.120 м² | 1000 мм | 996 мм | 200 мм | 196 мм | 71 | 14 |
| KRS 1000х225-АL-RAL9016 | 0.135 м² | 1000 мм | 996 мм | 225 мм | 221 мм | 71 | 16 |
| KRS 1000х250-АL-RAL9016 | 0.150 м² | 1000 мм | 996 мм | 250 мм | 246 мм | 71 | 18 |
| KRS 1000х300-АL-RAL9016 | 0.180 м² | 1000 мм | 996 мм | 300 мм | 296 мм | 71 | 21 |
| KRS 1000х325-АL-RAL9016 | 0.196 м² | 1000 мм | 996 мм | 325 мм | 321 мм | 71 | 23 |
| KRS 1000х350-АL-RAL9016 | 0.211 м² | 1000 мм | 996 мм | 350 мм | 346 мм | 71 | 25 |
| KRS 1000х400-АL-RAL9016 | 0.241 м² | 1000 мм | 996 мм | 400 мм | 396 мм | 71 | 29 |
| KRS 1000х425-АL-RAL9016 | 0.256 м² | 1000 мм | 996 мм | 425 мм | 421 мм | 71 | 30 |
| KRS 1000х450-АL-RAL9016 | 0.271 м² | 1000 мм | 996 мм | 450 мм | 446 мм | 71 | 32 |
| KRS 1000х500-АL-RAL9016 | 0.301 м² | 1000 мм | 996 мм | 500 мм | 496 мм | 71 | 36 |
| KRS 1000х525-АL-RAL9016 | 0.316 м² | 1000 мм | 996 мм | 525 мм | 521 мм | 71 | 38 |
| KRS 1000х550-АL-RAL9016 | 0.331 м² | 1000 мм | 996 мм | 550 мм | 546 мм | 71 | 39 |
| KRS 1000х600-АL-RAL9016 | 0.361 м² | 1000 мм | 996 мм | 600 мм | 596 мм | 71 | 43 |
| KRS 1000х625-АL-RAL9016 | 0.376 м² | 1000 мм | 996 мм | 625 мм | 621 мм | 71 | 45 |
| KRS 1025х100-АL-RAL9016 | 0.062 м² | 1025 мм | 1021 мм | 100 мм | 96 мм | 73 | 7 |
| KRS 1025х125-АL-RAL9016 | 0.077 м² | 1025 мм | 1021 мм | 125 мм | 121 мм | 73 | 9 |
| KRS 1025х150-АL-RAL9016 | 0.092 м² | 1025 мм | 1021 мм | 150 мм | 146 мм | 73 | 11 |
| KRS 1025х200-АL-RAL9016 | 0.123 м² | 1025 мм | 1021 мм | 200 мм | 196 мм | 73 | 14 |
| KRS 1025х225-АL-RAL9016 | 0.139 м² | 1025 мм | 1021 мм | 225 мм | 221 мм | 73 | 16 |
| KRS 1025х250-АL-RAL9016 | 0.154 м² | 1025 мм | 1021 мм | 250 мм | 246 мм | 73 | 18 |
| KRS 1025х300-АL-RAL9016 | 0.185 м² | 1025 мм | 1021 мм | 300 мм | 296 мм | 73 | 21 |
| KRS 1025х325-АL-RAL9016 | 0.200 м² | 1025 мм | 1021 мм | 325 мм | 321 мм | 73 | 23 |
| KRS 1025х350-АL-RAL9016 | 0.216 м² | 1025 мм | 1021 мм | 350 мм | 346 мм | 73 | 25 |
| KRS 1025х400-АL-RAL9016 | 0.247 м² | 1025 мм | 1021 мм | 400 мм | 396 мм | 73 | 29 |
| KRS 1025х425-АL-RAL9016 | 0.262 м² | 1025 мм | 1021 мм | 425 мм | 421 мм | 73 | 30 |
| KRS 1025х450-АL-RAL9016 | 0.277 м² | 1025 мм | 1021 мм | 450 мм | 446 мм | 73 | 32 |
| KRS 1025х500-АL-RAL9016 | 0.308 м² | 1025 мм | 1021 мм | 500 мм | 496 мм | 73 | 36 |
| KRS 1025х525-АL-RAL9016 | 0.324 м² | 1025 мм | 1021 мм | 525 мм | 521 мм | 73 | 38 |
| KRS 1025х550-АL-RAL9016 | 0.339 м² | 1025 мм | 1021 мм | 550 мм | 546 мм | 73 | 39 |
| KRS 1025х600-АL-RAL9016 | 0.370 м² | 1025 мм | 1021 мм | 600 мм | 596 мм | 73 | 43 |
| KRS 1025х625-АL-RAL9016 | 0.385 м² | 1025 мм | 1021 мм | 625 мм | 621 мм | 73 | 45 |
| KRS 1050х100-АL-RAL9016 | 0.063 м² | 1050 мм | 1046 мм | 100 мм | 96 мм | 75 | 7 |
| KRS 1050х125-АL-RAL9016 | 0.079 м² | 1050 мм | 1046 мм | 125 мм | 121 мм | 75 | 9 |
| KRS 1050х150-АL-RAL9016 | 0.095 м² | 1050 мм | 1046 мм | 150 мм | 146 мм | 75 | 11 |
| KRS 1050х200-АL-RAL9016 | 0.126 м² | 1050 мм | 1046 мм | 200 мм | 196 мм | 75 | 14 |
| KRS 1050х225-АL-RAL9016 | 0.142 м² | 1050 мм | 1046 мм | 225 мм | 221 мм | 75 | 16 |
| KRS 1050х250-АL-RAL9016 | 0.158 м² | 1050 мм | 1046 мм | 250 мм | 246 мм | 75 | 18 |
| KRS 1050х300-АL-RAL9016 | 0.190 м² | 1050 мм | 1046 мм | 300 мм | 296 мм | 75 | 21 |
| KRS 1050х325-АL-RAL9016 | 0.205 м² | 1050 мм | 1046 мм | 325 мм | 321 мм | 75 | 23 |
| KRS 1050х350-АL-RAL9016 | 0.221 м² | 1050 мм | 1046 мм | 350 мм | 346 мм | 75 | 25 |
| KRS 1050х400-АL-RAL9016 | 0.253 м² | 1050 мм | 1046 мм | 400 мм | 396 мм | 75 | 29 |
| KRS 1050х425-АL-RAL9016 | 0.268 м² | 1050 мм | 1046 мм | 425 мм | 421 мм | 75 | 30 |
| KRS 1050х450-АL-RAL9016 | 0.284 м² | 1050 мм | 1046 мм | 450 мм | 446 мм | 75 | 32 |
| KRS 1050х500-АL-RAL9016 | 0.316 м² | 1050 мм | 1046 мм | 500 мм | 496 мм | 75 | 36 |
| KRS 1050х525-АL-RAL9016 | 0.332 м² | 1050 мм | 1046 мм | 525 мм | 521 мм | 75 | 38 |
| KRS 1050х550-АL-RAL9016 | 0.347 м² | 1050 мм | 1046 мм | 550 мм | 546 мм | 75 | 39 |
| KRS 1050х600-АL-RAL9016 | 0.379 м² | 1050 мм | 1046 мм | 600 мм | 596 мм | 75 | 43 |
| KRS 1050х625-АL-RAL9016 | 0.395 м² | 1050 мм | 1046 мм | 625 мм | 621 мм | 75 | 45 |
| KRS 1100х100-АL-RAL9016 | 0.066 м² | 1100 мм | 1096 мм | 100 мм | 96 мм | 79 | 7 |
| KRS 1100х125-АL-RAL9016 | 0.083 м² | 1100 мм | 1096 мм | 125 мм | 121 мм | 79 | 9 |
| KRS 1100х150-АL-RAL9016 | 0.099 м² | 1100 мм | 1096 мм | 150 мм | 146 мм | 79 | 11 |
| KRS 1100х200-АL-RAL9016 | 0.132 м² | 1100 мм | 1096 мм | 200 мм | 196 мм | 79 | 14 |
| KRS 1100х225-АL-RAL9016 | 0.149 м² | 1100 мм | 1096 мм | 225 мм | 221 мм | 79 | 16 |
| KRS 1100х250-АL-RAL9016 | 0.165 м² | 1100 мм | 1096 мм | 250 мм | 246 мм | 79 | 18 |
| KRS 1100х300-АL-RAL9016 | 0.199 м² | 1100 мм | 1096 мм | 300 мм | 296 мм | 79 | 21 |
| KRS 1100х325-АL-RAL9016 | 0.215 м² | 1100 мм | 1096 мм | 325 мм | 321 мм | 79 | 23 |
| KRS 1100х350-АL-RAL9016 | 0.232 м² | 1100 мм | 1096 мм | 350 мм | 346 мм | 79 | 25 |
| KRS 1100х400-АL-RAL9016 | 0.265 м² | 1100 мм | 1096 мм | 400 мм | 396 мм | 79 | 29 |
| KRS 1100х425-АL-RAL9016 | 0.281 м² | 1100 мм | 1096 мм | 425 мм | 421 мм | 79 | 30 |
| KRS 1100х450-АL-RAL9016 | 0.298 м² | 1100 мм | 1096 мм | 450 мм | 446 мм | 79 | 32 |
| KRS 1100х500-АL-RAL9016 | 0.331 м² | 1100 мм | 1096 мм | 500 мм | 496 мм | 79 | 36 |
| KRS 1100х525-АL-RAL9016 | 0.347 м² | 1100 мм | 1096 мм | 525 мм | 521 мм | 79 | 38 |
| KRS 1100х550-АL-RAL9016 | 0.364 м² | 1100 мм | 1096 мм | 550 мм | 546 мм | 79 | 39 |
| KRS 1100х600-АL-RAL9016 | 0.397 м² | 1100 мм | 1096 мм | 600 мм | 596 мм | 79 | 43 |
| KRS 1100х625-АL-RAL9016 | 0.414 м² | 1100 мм | 1096 мм | 625 мм | 621 мм | 79 | 45 |
| KRS 1125х100-АL-RAL9016 | 0.068 м² | 1125 мм | 1121 мм | 100 мм | 96 мм | 80 | 7 |
| KRS 1125х125-АL-RAL9016 | 0.085 м² | 1125 мм | 1121 мм | 125 мм | 121 мм | 80 | 9 |
| KRS 1125х150-АL-RAL9016 | 0.102 м² | 1125 мм | 1121 мм | 150 мм | 146 мм | 80 | 11 |
| KRS 1125х200-АL-RAL9016 | 0.135 м² | 1125 мм | 1121 мм | 200 мм | 196 мм | 80 | 14 |
| KRS 1125х225-АL-RAL9016 | 0.152 м² | 1125 мм | 1121 мм | 225 мм | 221 мм | 80 | 16 |
| KRS 1125х250-АL-RAL9016 | 0.169 м² | 1125 мм | 1121 мм | 250 мм | 246 мм | 80 | 18 |
| KRS 1125х300-АL-RAL9016 | 0.203 м² | 1125 мм | 1121 мм | 300 мм | 296 мм | 80 | 21 |
| KRS 1125х325-АL-RAL9016 | 0.220 м² | 1125 мм | 1121 мм | 325 мм | 321 мм | 80 | 23 |
| KRS 1125х350-АL-RAL9016 | 0.237 м² | 1125 мм | 1121 мм | 350 мм | 346 мм | 80 | 25 |
| KRS 1125х400-АL-RAL9016 | 0.271 м² | 1125 мм | 1121 мм | 400 мм | 396 мм | 80 | 29 |
| KRS 1125х425-АL-RAL9016 | 0.288 м² | 1125 мм | 1121 мм | 425 мм | 421 мм | 80 | 30 |
| KRS 1125х450-АL-RAL9016 | 0.305 м² | 1125 мм | 1121 мм | 450 мм | 446 мм | 80 | 32 |
| KRS 1125х500-АL-RAL9016 | 0.338 м² | 1125 мм | 1121 мм | 500 мм | 496 мм | 80 | 36 |
| KRS 1125х525-АL-RAL9016 | 0.355 м² | 1125 мм | 1121 мм | 525 мм | 521 мм | 80 | 38 |
| KRS 1125х550-АL-RAL9016 | 0.372 м² | 1125 мм | 1121 мм | 550 мм | 546 мм | 80 | 39 |
| KRS 1125х600-АL-RAL9016 | 0.406 м² | 1125 мм | 1121 мм | 600 мм | 596 мм | 80 | 43 |
| KRS 1125х625-АL-RAL9016 | 0.423 м² | 1125 мм | 1121 мм | 625 мм | 621 мм | 80 | 45 |
| KRS 1150х100-АL-RAL9016 | 0.069 м² | 1150 мм | 1146 мм | 100 мм | 96 мм | 82 | 7 |
| KRS 1150х125-АL-RAL9016 | 0.086 м² | 1150 мм | 1146 мм | 125 мм | 121 мм | 82 | 9 |
| KRS 1150х150-АL-RAL9016 | 0.104 м² | 1150 мм | 1146 мм | 150 мм | 146 мм | 82 | 11 |
| KRS 1150х200-АL-RAL9016 | 0.138 м² | 1150 мм | 1146 мм | 200 мм | 196 мм | 82 | 14 |
| KRS 1150х225-АL-RAL9016 | 0.156 м² | 1150 мм | 1146 мм | 225 мм | 221 мм | 82 | 16 |
| KRS 1150х250-АL-RAL9016 | 0.173 м² | 1150 мм | 1146 мм | 250 мм | 246 мм | 82 | 18 |
| KRS 1150х300-АL-RAL9016 | 0.208 м² | 1150 мм | 1146 мм | 300 мм | 296 мм | 82 | 21 |
| KRS 1150х325-АL-RAL9016 | 0.225 м² | 1150 мм | 1146 мм | 325 мм | 321 мм | 82 | 23 |
| KRS 1150х350-АL-RAL9016 | 0.242 м² | 1150 мм | 1146 мм | 350 мм | 346 мм | 82 | 25 |
| KRS 1150х400-АL-RAL9016 | 0.277 м² | 1150 мм | 1146 мм | 400 мм | 396 мм | 82 | 29 |
| KRS 1150х425-АL-RAL9016 | 0.294 м² | 1150 мм | 1146 мм | 425 мм | 421 мм | 82 | 30 |
| KRS 1150х450-АL-RAL9016 | 0.311 м² | 1150 мм | 1146 мм | 450 мм | 446 мм | 82 | 32 |
| KRS 1150х500-АL-RAL9016 | 0.346 м² | 1150 мм | 1146 мм | 500 мм | 496 мм | 82 | 36 |
| KRS 1150х525-АL-RAL9016 | 0.363 м² | 1150 мм | 1146 мм | 525 мм | 521 мм | 82 | 38 |
| KRS 1150х550-АL-RAL9016 | 0.381 м² | 1150 мм | 1146 мм | 550 мм | 546 мм | 82 | 39 |
| KRS 1150х600-АL-RAL9016 | 0.415 м² | 1150 мм | 1146 мм | 600 мм | 596 мм | 82 | 43 |
| KRS 1150х625-АL-RAL9016 | 0.432 м² | 1150 мм | 1146 мм | 625 мм | 621 мм | 82 | 45 |
| KRS 1200х100-АL-RAL9016 | 0.072 м² | 1200 мм | 1196 мм | 100 мм | 96 мм | 86 | 7 |
| KRS 1200х125-АL-RAL9016 | 0.090 м² | 1200 мм | 1196 мм | 125 мм | 121 мм | 86 | 9 |
| KRS 1200х150-АL-RAL9016 | 0.108 м² | 1200 мм | 1196 мм | 150 мм | 146 мм | 86 | 11 |
| KRS 1200х200-АL-RAL9016 | 0.144 м² | 1200 мм | 1196 мм | 200 мм | 196 мм | 86 | 14 |
| KRS 1200х225-АL-RAL9016 | 0.162 м² | 1200 мм | 1196 мм | 225 мм | 221 мм | 86 | 16 |
| KRS 1200х250-АL-RAL9016 | 0.180 м² | 1200 мм | 1196 мм | 250 мм | 246 мм | 86 | 18 |
| KRS 1200х300-АL-RAL9016 | 0.217 м² | 1200 мм | 1196 мм | 300 мм | 296 мм | 86 | 21 |
| KRS 1200х325-АL-RAL9016 | 0.235 м² | 1200 мм | 1196 мм | 325 мм | 321 мм | 86 | 23 |
| KRS 1200х350-АL-RAL9016 | 0.253 м² | 1200 мм | 1196 мм | 350 мм | 346 мм | 86 | 25 |
| KRS 1200х400-АL-RAL9016 | 0.289 м² | 1200 мм | 1196 мм | 400 мм | 396 мм | 86 | 29 |
| KRS 1200х425-АL-RAL9016 | 0.307 м² | 1200 мм | 1196 мм | 425 мм | 421 мм | 86 | 30 |
| KRS 1200х450-АL-RAL9016 | 0.325 м² | 1200 мм | 1196 мм | 450 мм | 446 мм | 86 | 32 |
| KRS 1200х500-АL-RAL9016 | 0.361 м² | 1200 мм | 1196 мм | 500 мм | 496 мм | 86 | 36 |
| KRS 1200х525-АL-RAL9016 | 0.379 м² | 1200 мм | 1196 мм | 525 мм | 521 мм | 86 | 38 |
| KRS 1200х550-АL-RAL9016 | 0.397 м² | 1200 мм | 1196 мм | 550 мм | 546 мм | 86 | 39 |
| KRS 1200х600-АL-RAL9016 | 0.433 м² | 1200 мм | 1196 мм | 600 мм | 596 мм | 86 | 43 |
| KRS 1200х625-АL-RAL9016 | 0.451 м² | 1200 мм | 1196 мм | 625 мм | 621 мм | 86 | 45 |
| KRS 1225х100-АL-RAL9016 | 0.074 м² | 1225 мм | 1221 мм | 100 мм | 96 мм | 88 | 7 |
| KRS 1225х125-АL-RAL9016 | 0.092 м² | 1225 мм | 1221 мм | 125 мм | 121 мм | 88 | 9 |
| KRS 1225х150-АL-RAL9016 | 0.111 м² | 1225 мм | 1221 мм | 150 мм | 146 мм | 88 | 11 |
| KRS 1225х200-АL-RAL9016 | 0.147 м² | 1225 мм | 1221 мм | 200 мм | 196 мм | 88 | 14 |
| KRS 1225х225-АL-RAL9016 | 0.166 м² | 1225 мм | 1221 мм | 225 мм | 221 мм | 88 | 16 |
| KRS 1225х250-АL-RAL9016 | 0.184 м² | 1225 мм | 1221 мм | 250 мм | 246 мм | 88 | 18 |
| KRS 1225х300-АL-RAL9016 | 0.221 м² | 1225 мм | 1221 мм | 300 мм | 296 мм | 88 | 21 |
| KRS 1225х325-АL-RAL9016 | 0.240 м² | 1225 мм | 1221 мм | 325 мм | 321 мм | 88 | 23 |
| KRS 1225х350-АL-RAL9016 | 0.258 м² | 1225 мм | 1221 мм | 350 мм | 346 мм | 88 | 25 |
| KRS 1225х400-АL-RAL9016 | 0.295 м² | 1225 мм | 1221 мм | 400 мм | 396 мм | 88 | 29 |
| KRS 1225х425-АL-RAL9016 | 0.313 м² | 1225 мм | 1221 мм | 425 мм | 421 мм | 88 | 30 |
| KRS 1225х450-АL-RAL9016 | 0.332 м² | 1225 мм | 1221 мм | 450 мм | 446 мм | 88 | 32 |
| KRS 1225х500-АL-RAL9016 | 0.368 м² | 1225 мм | 1221 мм | 500 мм | 496 мм | 88 | 36 |
| KRS 1225х525-АL-RAL9016 | 0.387 м² | 1225 мм | 1221 мм | 525 мм | 521 мм | 88 | 38 |
| KRS 1225х550-АL-RAL9016 | 0.405 м² | 1225 мм | 1221 мм | 550 мм | 546 мм | 88 | 39 |
| KRS 1225х600-АL-RAL9016 | 0.442 м² | 1225 мм | 1221 мм | 600 мм | 596 мм | 88 | 43 |
| KRS 1225х625-АL-RAL9016 | 0.461 м² | 1225 мм | 1221 мм | 625 мм | 621 мм | 88 | 45 |

note: column(s) folded — value = type name in every type: Комментарии к типоразмеру
